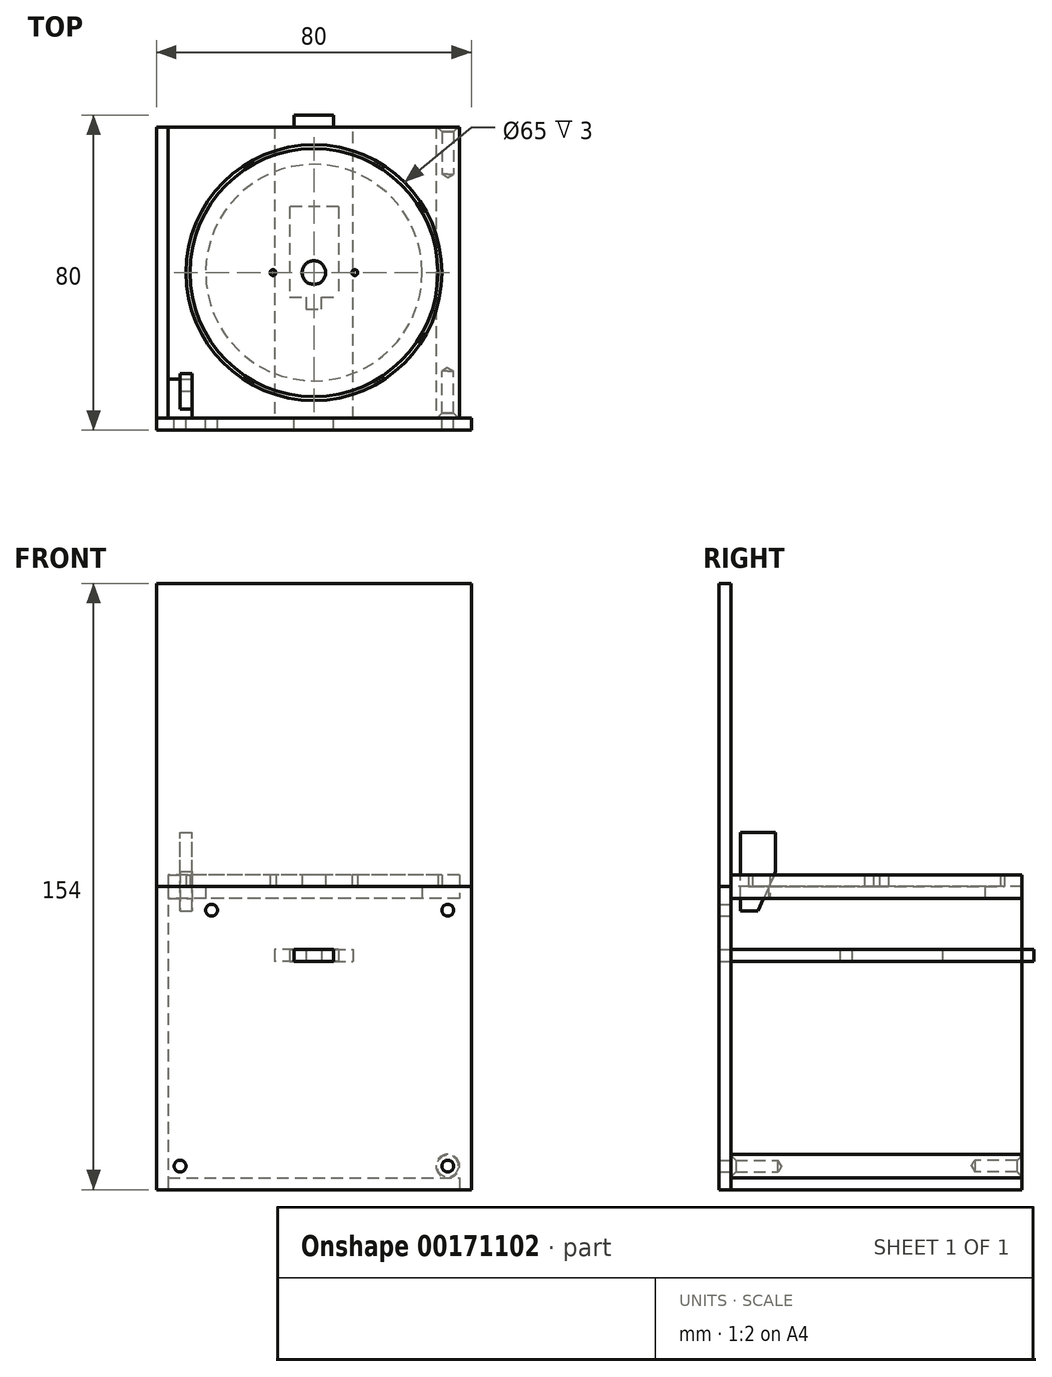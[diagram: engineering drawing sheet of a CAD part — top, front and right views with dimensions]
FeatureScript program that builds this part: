
annotation { "Feature Type Name" : "Feature", "Feature Type Description" : "" }
export const myFeature = defineFeature(function(context is Context, id is Id, definition is map)
    precondition{}
    {
        {
            assignVariable(context, id + "F0", {"name" : "thickness", "anyValue" : 3});
        }
        {
            assignVariable(context, id + "F1", {"name" : "depth", "anyValue" : 80});
        }
        {
            assignVariable(context, id + "F2", {"name" : "beamdiameter", "anyValue" : 6});
        }
        {
            assignVariable(context, id + "F3", {"name" : "beamthreaddiameter", "anyValue" : 3});
        }
        {
            var Q0;
            Q0=qCreatedBy(makeId("Top.planeOp"),FACE);
            var sketch = newSketch(context, id + "F4", { "sketchPlane" : qUnion([Q0])});
            skLineSegment(sketch, "E0.bottom", {"start": v(37, 37) * mm, "end": v(-37, 37) * mm});
            skLineSegment(sketch, "E0.top", {"start": v(37, -37) * mm, "end": v(-37, -37) * mm});
            skLineSegment(sketch, "E0.left", {"start": v(37, 37) * mm, "end": v(37, -37) * mm});
            skLineSegment(sketch, "E0.right", {"start": v(-37, 37) * mm, "end": v(-37, -37) * mm});
            skPoint(sketch, "E0.middle", {"position": v(0, 0) * mm});
            skCircle(sketch, "E1", {"center": v(0, 0) * mm, "radius": 27.5 * mm});
            skLineSegment(sketch, "E2.bottom", {"start": v(-37, -37) * mm, "end": v(-31, -37) * mm});
            skLineSegment(sketch, "E2.top", {"start": v(-37, -27) * mm, "end": v(-31, -27) * mm});
            skLineSegment(sketch, "E2.left", {"start": v(-37, -37) * mm, "end": v(-37, -27) * mm});
            skLineSegment(sketch, "E2.right", {"start": v(-31, -37) * mm, "end": v(-31, -27) * mm});
            skSolve(sketch);
        }
        {
            var Q0;
            Q0=makeQuery(id+"F4.imprint","IMPRINT",FACE,{"disambiguationData":[TD([[makeQuery(id+"F4.imprint","IMPRINT",EDGE,{"derivedFrom":sQuery(id+"F4.wireOp",EDGE,"E0.bottom")}),1.0]])]});
            extrude(context, id + "F5", {"entities" : qUnion([Q0]), "depth" : (getVariable(context, 'thickness')) * mm});
        }
        {
            var Q0;
            Q0=makeQuery(id+"F5.opExtrude","CAP_FACE",FACE,{"disambiguationData":[OSD([sQuery(id+"F4.wireOp",EDGE,"E0.bottom"),sQuery(id+"F4.wireOp",EDGE,"E0.top"),sQuery(id+"F4.wireOp",EDGE,"E0.left"),sQuery(id+"F4.wireOp",EDGE,"E0.right"),sQuery(id+"F4.wireOp",EDGE,"E1")])],"isStart":false});
            var sketch = newSketch(context, id + "F6", { "sketchPlane" : qUnion([Q0])});
            skCircle(sketch, "E3", {"center": v(0, 0) * mm, "radius": 32.5 * mm});
            skSolve(sketch);
        }
        {
            var Q0;
            Q0=makeQuery(id+"F6.imprint","IMPRINT",FACE,{"disambiguationData":[TD([[makeQuery(id+"F6.imprint","IMPRINT",EDGE,{"derivedFrom":sQuery(id+"F6.wireOp",EDGE,"E3")}),-1.0]])]});
            extrude(context, id + "F7", {"entities" : qUnion([Q0]), "operationType" : NewBodyOperationType.ADD, "depth" : (getVariable(context, 'thickness')) * mm});
        }
        {
            var Q0;
            Q0=makeQuery(id+"F5.opExtrude","CAP_FACE",FACE,{"disambiguationData":[OSD([sQuery(id+"F4.wireOp",EDGE,"E0.bottom"),sQuery(id+"F4.wireOp",EDGE,"E0.top"),sQuery(id+"F4.wireOp",EDGE,"E0.left"),sQuery(id+"F4.wireOp",EDGE,"E0.right"),sQuery(id+"F4.wireOp",EDGE,"E1"),sQuery(id+"F4.wireOp",EDGE,"E2.top"),sQuery(id+"F4.wireOp",EDGE,"E2.right")])],"isStart":false});
            var sketch = newSketch(context, id + "F8", { "sketchPlane" : qUnion([Q0])});
            skCircle(sketch, "E4", {"center": v(0, 0) * mm, "radius": 31.5 * mm});
            skCircle(sketch, "E5", {"center": v(0, 0) * mm, "radius": 3 * mm});
            skLineSegment(sketch, "E6", {"start": v(-37.17, 0) * mm, "end": v(37.93, 0) * mm, "construction": true});
            skCircle(sketch, "E7", {"center": v(10.4, 0) * mm, "radius": 0.75 * mm});
            skCircle(sketch, "E8", {"center": v(-10.4, 0) * mm, "radius": 0.75 * mm});
            skLineSegment(sketch, "E9", {"start": v(0, -37.86) * mm, "end": v(0, 39.6) * mm, "construction": true});
            skSolve(sketch);
        }
        {
            var Q0;
            Q0 = qSketchRegion(id + "F8", true);
            extrude(context, id + "F9", {"entities" : qUnion([Q0]), "depth" : (getVariable(context, 'thickness')) * mm});
        }
        {
            var Q0;
            {var subQ0=sQuery(id+"F4.wireOp",EDGE,"E0.right");Q0=makeQuery(id+"F7.boolean.opBoolean","MERGE",FACE,{"derivedFrom":[makeQuery(id+"F5.opExtrude","SWEPT_FACE",FACE,{"disambiguationData":[OSD([subQ0])]}),makeQuery(id+"F7.opExtrude","SWEPT_FACE",FACE,{"disambiguationData":[OSD([subQ0])]})]});}
            var sketch = newSketch(context, id + "F10", { "sketchPlane" : qUnion([Q0])});
            skLineSegment(sketch, "E10.bottom", {"start": v(-37, 3) * mm, "end": v(37, 3) * mm});
            skLineSegment(sketch, "E10.top", {"start": v(-37, -74) * mm, "end": v(37, -74) * mm});
            skLineSegment(sketch, "E10.left", {"start": v(-37, 3) * mm, "end": v(-37, -74) * mm});
            skLineSegment(sketch, "E10.right", {"start": v(37, 3) * mm, "end": v(37, -74) * mm});
            skSolve(sketch);
        }
        {
            var Q0;
            {var subQ4=sQuery(id+"F10.wireOp",EDGE,"E10.top");Q0=makeQuery(id+"F10.imprint","IMPRINT",FACE,{"disambiguationData":[TD([[makeQuery(id+"F10.imprint","IMPRINT",EDGE,{"derivedFrom":subQ4}),1.0]])]});}
            var Q1;
            {var subQ2=sQuery(id+"F4.wireOp",EDGE,"E0.right");var subQ8=makeQuery(id+"F5.opExtrude","CAP_EDGE",EDGE,{"disambiguationData":[OSD([subQ2])],"isStart":true});Q1=makeQuery(id+"F10.imprint","IMPRINT",FACE,{"disambiguationData":[TD([[makeQuery(id+"F10.imprint","IMPRINT",EDGE,{"derivedFrom":subQ8}),1.0]])]});}
            extrude(context, id + "F11", {"entities" : qUnion([Q0, Q1]), "depth" : (getVariable(context, 'thickness')) * mm});
        }
        {
            var Q0;
            Q0=makeQuery(id+"F11.opExtrude","SWEPT_FACE",FACE,{"disambiguationData":[OSD([sQuery(id+"F10.wireOp",EDGE,"E10.top")])]});
            var sketch = newSketch(context, id + "F12", { "sketchPlane" : qUnion([Q0])});
            skLineSegment(sketch, "E11.bottom", {"start": v(-37, 37) * mm, "end": v(37, 37) * mm});
            skLineSegment(sketch, "E11.top", {"start": v(-37, -37) * mm, "end": v(37, -37) * mm});
            skLineSegment(sketch, "E11.left", {"start": v(-37, 37) * mm, "end": v(-37, -37) * mm});
            skLineSegment(sketch, "E11.right", {"start": v(37, 37) * mm, "end": v(37, -37) * mm});
            skSolve(sketch);
        }
        {
            var Q0;
            Q0 = qSketchRegion(id + "F12", true);
            extrude(context, id + "F13", {"entities" : qUnion([Q0]), "oppositeDirection" : true, "depth" : (getVariable(context, 'thickness')) * mm});
        }
        {
            var Q0;
            Q0=makeQuery(id+"F11.opExtrude","SWEPT_FACE",FACE,{"disambiguationData":[OSD([sQuery(id+"F10.wireOp",EDGE,"E10.right")])]});
            var sketch = newSketch(context, id + "F14", { "sketchPlane" : qUnion([Q0])});
            skLineSegment(sketch, "E12.bottom", {"start": v(-40, -74) * mm, "end": v(40, -74) * mm});
            skLineSegment(sketch, "E12.top", {"start": v(-40, 3) * mm, "end": v(40, 3) * mm});
            skLineSegment(sketch, "E12.left", {"start": v(-40, -74) * mm, "end": v(-40, 3) * mm});
            skLineSegment(sketch, "E12.right", {"start": v(40, -74) * mm, "end": v(40, 3) * mm});
            skCircle(sketch, "E13", {"center": v(-34, -68) * mm, "radius": 1.5 * mm});
            skCircle(sketch, "E14", {"center": v(34, -3) * mm, "radius": 1.5 * mm});
            skCircle(sketch, "E15", {"center": v(34, -68) * mm, "radius": 1.5 * mm});
            skLineSegment(sketch, "E16.bottom", {"start": v(-5, -16) * mm, "end": v(5, -16) * mm});
            skLineSegment(sketch, "E16.top", {"start": v(-5, -13) * mm, "end": v(5, -13) * mm});
            skLineSegment(sketch, "E16.left", {"start": v(-5, -16) * mm, "end": v(-5, -13) * mm});
            skLineSegment(sketch, "E16.right", {"start": v(5, -16) * mm, "end": v(5, -13) * mm});
            skPoint(sketch, "E16.middle", {"position": v(0, -14.5) * mm});
            skCircle(sketch, "E17", {"center": v(-26, -3) * mm, "radius": 1.5 * mm});
            skSolve(sketch);
        }
        {
            var Q0;
            Q0 = qSketchRegion(id + "F14", true);
            extrude(context, id + "F15", {"entities" : qUnion([Q0]), "depth" : (getVariable(context, 'thickness')) * mm});
        }
        {
            var Q0;
            Q0=makeQuery(id+"F15.opExtrude","CAP_FACE",FACE,{"disambiguationData":[OSD([sQuery(id+"F14.wireOp",EDGE,"E12.bottom"),sQuery(id+"F14.wireOp",EDGE,"E12.top"),sQuery(id+"F14.wireOp",EDGE,"E12.left"),sQuery(id+"F14.wireOp",EDGE,"E12.right"),sQuery(id+"F14.wireOp",EDGE,"E13"),sQuery(id+"F14.wireOp",EDGE,"E14"),sQuery(id+"F14.wireOp",EDGE,"E15")])],"isStart":true});
            var sketch = newSketch(context, id + "F16", { "sketchPlane" : qUnion([Q0])});
            skCircle(sketch, "E18", {"center": v(-34, -68) * mm, "radius": 3 * mm});
            skSolve(sketch);
        }
        {
            var Q0;
            Q0 = qSketchRegion(id + "F16", true);
            extrude(context, id + "F17", {"entities" : qUnion([Q0]), "depth" : (getVariable(context, 'depth') - (getVariable(context, 'thickness') * 2)) * mm});
        }
        {
            var Q0;
            Q0=makeQuery(id+"F17.opExtrude","CAP_FACE",FACE,{"disambiguationData":[OSD([sQuery(id+"F16.wireOp",EDGE,"E18")])],"isStart":false});
            var sketch = newSketch(context, id + "F18", { "sketchPlane" : qUnion([Q0])});
            skPoint(sketch, "E19", {"position": v(-34, -68) * mm});
            skSolve(sketch);
        }
        {
            var Q0;
            Q0=sQuery(id+"F18.wireOp",VERTEX,"E19");
            var Q1;
            Q1=makeQuery(id+"F17.opExtrude","SWEPT_BODY",BODY,{"disambiguationData":[OSD([sQuery(id+"F16.wireOp",EDGE,"E18")])]});
            hole(context, id + "F19", {"style" : HoleStyle.C_SINK, "endStyle" : HoleEndStyle.BLIND, "holeDiameter" : (getVariable(context, 'beamthreaddiameter')) * mm, "cSinkDiameter" : (getVariable(context, 'beamdiameter') - 0.5) * mm, "cSinkAngle" : 90 * degree, "holeDepth" : 12 * mm, "locations" : qUnion([Q0]), "scope" : qUnion([Q1]), "startStyle" : HoleStartStyle.PART});
        }
        {
            var Q0;
            Q0=makeQuery(id+"F17.opExtrude","CAP_FACE",FACE,{"disambiguationData":[OSD([sQuery(id+"F16.wireOp",EDGE,"E18")])],"isStart":true});
            var sketch = newSketch(context, id + "F20", { "sketchPlane" : qUnion([Q0])});
            skPoint(sketch, "E20", {"position": v(34, -68) * mm});
            skSolve(sketch);
        }
        {
            var Q0;
            Q0=sQuery(id+"F20.wireOp",VERTEX,"E20");
            var Q1;
            Q1=makeQuery(id+"F17.opExtrude","SWEPT_BODY",BODY,{"disambiguationData":[OSD([sQuery(id+"F16.wireOp",EDGE,"E18")])]});
            hole(context, id + "F21", {"style" : HoleStyle.C_SINK, "endStyle" : HoleEndStyle.BLIND, "holeDiameter" : (getVariable(context, 'beamthreaddiameter')) * mm, "cSinkDiameter" : (getVariable(context, 'beamdiameter') - 0.5) * mm, "cSinkAngle" : 90 * degree, "holeDepth" : 12 * mm, "locations" : qUnion([Q0]), "scope" : qUnion([Q1]), "startStyle" : HoleStartStyle.PART});
        }
        {
            var Q0;
            Q0=makeQuery(id+"F15.opExtrude","SWEPT_FACE",FACE,{"disambiguationData":[OSD([sQuery(id+"F14.wireOp",EDGE,"E16.bottom")])]});
            var sketch = newSketch(context, id + "F22", { "sketchPlane" : qUnion([Q0])});
            skLineSegment(sketch, "E21.0", {"start": v(5, -40) * mm, "end": v(5, -37) * mm});
            skLineSegment(sketch, "E22.0", {"start": v(-5, -40) * mm, "end": v(-5, -37) * mm});
            skLineSegment(sketch, "E23.0", {"start": v(-5, -40) * mm, "end": v(5, -40) * mm});
            skLineSegment(sketch, "E24", {"start": v(5, -37) * mm, "end": v(10, -37) * mm});
            skLineSegment(sketch, "E25", {"start": v(10, -37) * mm, "end": v(10, 37) * mm});
            skLineSegment(sketch, "E26", {"start": v(10, 37) * mm, "end": v(5, 37) * mm});
            skLineSegment(sketch, "E27", {"start": v(5, 37) * mm, "end": v(5, 40) * mm});
            skLineSegment(sketch, "E28", {"start": v(5, 40) * mm, "end": v(-5, 40) * mm});
            skLineSegment(sketch, "E29", {"start": v(-5, 40) * mm, "end": v(-5, 37) * mm});
            skLineSegment(sketch, "E30", {"start": v(-5, 37) * mm, "end": v(-10, 37) * mm});
            skLineSegment(sketch, "E31", {"start": v(-10, 37) * mm, "end": v(-10, -37) * mm});
            skLineSegment(sketch, "E32", {"start": v(-10, -37) * mm, "end": v(-5, -37) * mm});
            skLineSegment(sketch, "E33.bottom", {"start": v(6.2, 16.75) * mm, "end": v(-6.2, 16.75) * mm});
            skLineSegment(sketch, "E33.top", {"start": v(6.2, -6.25) * mm, "end": v(-6.2, -6.25) * mm, "construction": true});
            skLineSegment(sketch, "E33.left", {"start": v(6.2, 16.75) * mm, "end": v(6.2, -6.25) * mm});
            skLineSegment(sketch, "E33.right", {"start": v(-6.2, 16.75) * mm, "end": v(-6.2, -6.25) * mm});
            skPoint(sketch, "E33.middle", {"position": v(0, 0) * mm});
            skLineSegment(sketch, "E34", {"start": v(-10, 0) * mm, "end": v(10, 0) * mm, "construction": true});
            skLineSegment(sketch, "E35", {"start": v(0, -37) * mm, "end": v(0, 34.95) * mm, "construction": true});
            skLineSegment(sketch, "E36", {"start": v(-6.2, -6.25) * mm, "end": v(-2, -6.25) * mm});
            skLineSegment(sketch, "E37", {"start": v(-2, -6.25) * mm, "end": v(-2, -9.25) * mm});
            skLineSegment(sketch, "E38", {"start": v(-2, -9.25) * mm, "end": v(2, -9.25) * mm});
            skLineSegment(sketch, "E39", {"start": v(2, -9.25) * mm, "end": v(2, -6.25) * mm});
            skLineSegment(sketch, "E40", {"start": v(2, -6.25) * mm, "end": v(6.2, -6.25) * mm});
            skSolve(sketch);
        }
        {
            var Q0;
            Q0 = qSketchRegion(id + "F22", true);
            extrude(context, id + "F23", {"entities" : qUnion([Q0]), "depth" : (getVariable(context, 'thickness')) * mm});
        }
        {
            var Q0;
            {var subQ0=sQuery(id+"F4.wireOp",EDGE,"E2.right");Q0=makeQuery(id+"F7.boolean.opBoolean","MERGE",FACE,{"derivedFrom":[makeQuery(id+"F5.opExtrude","SWEPT_FACE",FACE,{"disambiguationData":[OSD([subQ0])]}),makeQuery(id+"F7.opExtrude","SWEPT_FACE",FACE,{"disambiguationData":[OSD([subQ0])]})]});}
            var sketch = newSketch(context, id + "F24", { "sketchPlane" : qUnion([Q0])});
            skLineSegment(sketch, "E41.bottom", {"start": v(25.61, -3.2) * mm, "end": v(34.61, -3.2) * mm, "construction": true});
            skLineSegment(sketch, "E41.top", {"start": v(25.61, 16.8) * mm, "end": v(34.61, 16.8) * mm});
            skLineSegment(sketch, "E41.left", {"start": v(25.61, -3.2) * mm, "end": v(25.61, 16.8) * mm, "construction": true});
            skLineSegment(sketch, "E41.right", {"start": v(34.61, -3.2) * mm, "end": v(34.61, 16.8) * mm});
            skLineSegment(sketch, "E42", {"start": v(25.61, 6.8) * mm, "end": v(30.11, -3.2) * mm});
            skLineSegment(sketch, "E43", {"start": v(25.61, 6.8) * mm, "end": v(25.61, 16.8) * mm});
            skLineSegment(sketch, "E44", {"start": v(30.11, -3.2) * mm, "end": v(34.61, -3.2) * mm});
            skSolve(sketch);
        }
        {
            var Q0;
            Q0 = qSketchRegion(id + "F24", true);
            extrude(context, id + "F25", {"entities" : qUnion([Q0]), "depth" : (getVariable(context, 'thickness')) * mm});
        }
        {
            var Q0;
            {var subQ0=sQuery(id+"F4.wireOp",EDGE,"E0.top");Q0=makeQuery(id+"F7.boolean.opBoolean","MERGE",FACE,{"derivedFrom":[makeQuery(id+"F5.opExtrude","SWEPT_FACE",FACE,{"disambiguationData":[OSD([subQ0])]}),makeQuery(id+"F7.opExtrude","SWEPT_FACE",FACE,{"disambiguationData":[OSD([subQ0])]})]});}
            var sketch = newSketch(context, id + "F26", { "sketchPlane" : qUnion([Q0])});
            skLineSegment(sketch, "E45.bottom", {"start": v(-40, 80) * mm, "end": v(40, 80) * mm});
            skLineSegment(sketch, "E45.top", {"start": v(-40, 3) * mm, "end": v(40, 3) * mm});
            skLineSegment(sketch, "E45.left", {"start": v(-40, 80) * mm, "end": v(-40, 3) * mm});
            skLineSegment(sketch, "E45.right", {"start": v(40, 80) * mm, "end": v(40, 3) * mm});
            skPoint(sketch, "E45.middle", {"position": v(0, 41.5) * mm});
            skPoint(sketch, "E46.0", {"position": v(-40, 3) * mm});
            skSolve(sketch);
        }
        {
            var Q0;
            Q0 = qSketchRegion(id + "F26", true);
            extrude(context, id + "F27", {"entities" : qUnion([Q0]), "depth" : (getVariable(context, 'thickness')) * mm});
        }
    });
